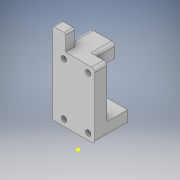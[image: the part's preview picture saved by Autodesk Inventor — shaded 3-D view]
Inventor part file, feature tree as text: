
AUTODESK INVENTOR PART (.ipt)
format: ipt  version: 2018 (Build 220112000, 112)  size: 184,832 bytes
history: native  units: in
note: dims shown in document units (in); Inventor stores cm internally (conversion verified against a paired STEP export)
features: sketch x7, plane x4, other x3
ambient origin geometry x8: Origin, YZ Plane, XZ Plane, XY Plane, X Axis, Y Axis, Z Axis, Center Point
bodies: Solid1 (feature_tree)
feature tree (14):
  other  "SyringeMotorBase.ipt"
  other  "Solid1::SyringeMotorBase.ipt"
  other  "TaggingFeature1"
  sketch  "Sketch1"  dims[d0=0.3937in]
  sketch  "Sketch2"
  sketch  "Sketch3"
  sketch  "Sketch4"
  sketch  "Sketch5"
  sketch  "Sketch6"
  sketch  "Sketch7"
  plane  "Work Plane1"
  plane  "Work Plane2"
  plane  "Work Plane3"
  plane  "Work Plane4"
